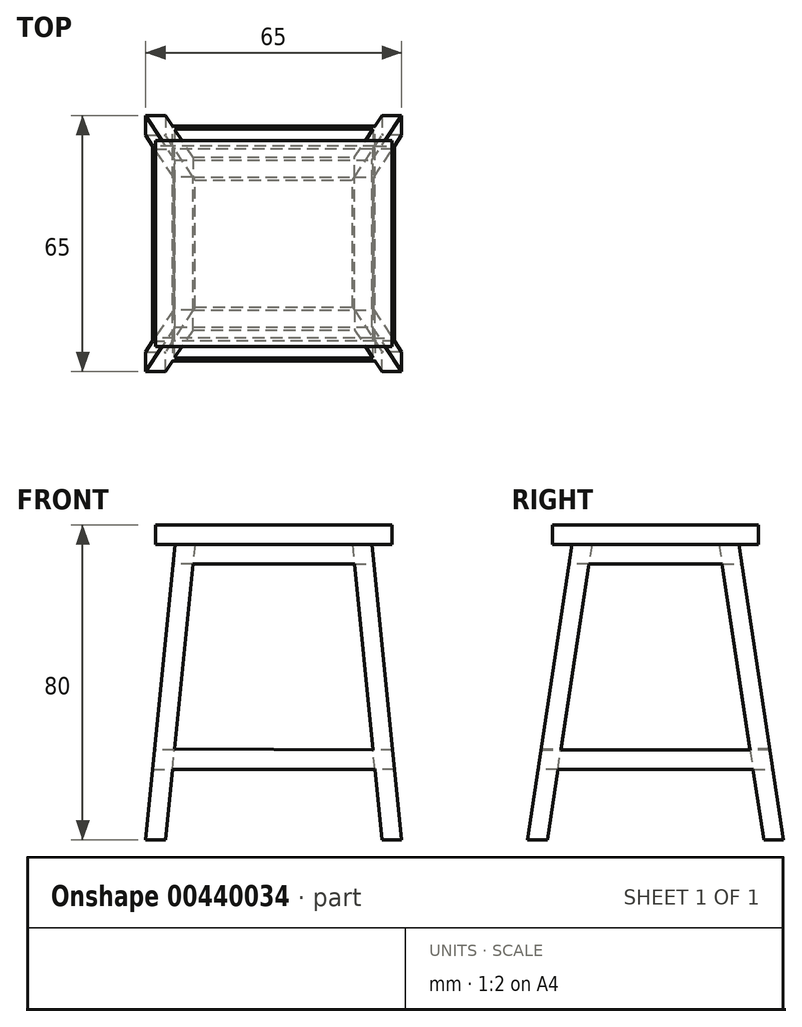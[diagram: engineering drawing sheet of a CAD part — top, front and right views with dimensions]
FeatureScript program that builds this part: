
annotation { "Feature Type Name" : "Feature", "Feature Type Description" : "" }
export const myFeature = defineFeature(function(context is Context, id is Id, definition is map)
    precondition{}
    {
        {
            var Q0;
            Q0=qCreatedBy(makeId("Top.planeOp"),FACE);
            var sketch = newSketch(context, id + "F0", { "sketchPlane" : qUnion([Q0])});
            skLineSegment(sketch, "E0.bottom", {"start": v(-30, 26.18) * mm, "end": v(30, 26.18) * mm});
            skLineSegment(sketch, "E0.top", {"start": v(-30, -26.18) * mm, "end": v(30, -26.18) * mm});
            skLineSegment(sketch, "E0.left", {"start": v(-30, 26.18) * mm, "end": v(-30, -26.18) * mm});
            skLineSegment(sketch, "E0.right", {"start": v(30, 26.18) * mm, "end": v(30, -26.18) * mm});
            skPoint(sketch, "E0.middle", {"position": v(0, 0) * mm});
            skSolve(sketch);
        }
        {
            var Q0;
            Q0 = qSketchRegion(id + "F0", true);
            extrude(context, id + "F1", {"entities" : qUnion([Q0]), "depth" : 5 * mm});
        }
        {
            var Q0;
            Q0=qCreatedBy(makeId("Top.planeOp"),FACE);
            var sketch = newSketch(context, id + "F2", { "sketchPlane" : qUnion([Q0])});
            skLineSegment(sketch, "E1.bottom", {"start": v(-25, -21.18) * mm, "end": v(-20, -21.18) * mm});
            skLineSegment(sketch, "E1.top", {"start": v(-25, -16.18) * mm, "end": v(-20, -16.18) * mm});
            skLineSegment(sketch, "E1.left", {"start": v(-25, -21.18) * mm, "end": v(-25, -16.18) * mm});
            skLineSegment(sketch, "E1.right", {"start": v(-20, -21.18) * mm, "end": v(-20, -16.18) * mm});
            skPoint(sketch, "E1.middle", {"position": v(-22.5, -18.68) * mm});
            skSolve(sketch);
        }
        {
            var Q0;
            Q0=qCreatedBy(makeId("Top.planeOp"),FACE);
            cPlane(context, id + "F3", {"entities" : qUnion([Q0]), "cplaneType" : CPlaneType.OFFSET, "offset" : 75 * mm, "oppositeDirection" : true, "width" : 150 * mm, "height" : 150 * mm});
        }
        {
            var Q0;
            Q0=qCreatedBy(id+"F3.planeOp",FACE);
            var sketch = newSketch(context, id + "F4", { "sketchPlane" : qUnion([Q0])});
            skLineSegment(sketch, "E2.bottom", {"start": v(-32.5, -32.5) * mm, "end": v(32.5, -32.5) * mm, "construction": true});
            skLineSegment(sketch, "E2.top", {"start": v(-32.5, 32.5) * mm, "end": v(32.5, 32.5) * mm, "construction": true});
            skLineSegment(sketch, "E2.left", {"start": v(-32.5, -32.5) * mm, "end": v(-32.5, 32.5) * mm, "construction": true});
            skLineSegment(sketch, "E2.right", {"start": v(32.5, -32.5) * mm, "end": v(32.5, 32.5) * mm, "construction": true});
            skPoint(sketch, "E2.middle", {"position": v(0, 0) * mm});
            skLineSegment(sketch, "E3.bottom", {"start": v(-32.5, -32.5) * mm, "end": v(-27.5, -32.5) * mm});
            skLineSegment(sketch, "E3.top", {"start": v(-32.5, -27.5) * mm, "end": v(-27.5, -27.5) * mm});
            skLineSegment(sketch, "E3.left", {"start": v(-32.5, -32.5) * mm, "end": v(-32.5, -27.5) * mm});
            skLineSegment(sketch, "E3.right", {"start": v(-27.5, -32.5) * mm, "end": v(-27.5, -27.5) * mm});
            skSolve(sketch);
        }
        {
            var Q1;
            Q1=makeQuery(id+"F2.imprint","IMPRINT",FACE,{"disambiguationData":[TD([[makeQuery(id+"F2.imprint","IMPRINT",EDGE,{"derivedFrom":sQuery(id+"F2.wireOp",EDGE,"E1.bottom")}),1.0]])]});
            var Q2;
            Q2=makeQuery(id+"F4.imprint","IMPRINT",FACE,{"disambiguationData":[TD([[makeQuery(id+"F4.imprint","IMPRINT",EDGE,{"derivedFrom":sQuery(id+"F4.wireOp",EDGE,"E3.bottom")}),1.0]])]});
            loft(context, id + "F5", {"sheetProfilesArray" : [{ "sheetProfileEntities" : qUnion([Q1]) }, { "sheetProfileEntities" : qUnion([Q2]) }]});
        }
        {
            var Q0;
            Q0=makeQuery(id+"F5.opLoft","SWEPT_BODY",BODY,{"disambiguationData":[OSD([makeQuery(id+"F2.imprint","IMPRINT",FACE,{"disambiguationData":[TD([[makeQuery(id+"F2.imprint","IMPRINT",EDGE,{"derivedFrom":sQuery(id+"F2.wireOp",EDGE,"E1.bottom")}),1.0]])]}),makeQuery(id+"F4.imprint","IMPRINT",FACE,{"disambiguationData":[TD([[makeQuery(id+"F4.imprint","IMPRINT",EDGE,{"derivedFrom":sQuery(id+"F4.wireOp",EDGE,"E3.bottom")}),1.0]])]})])]});
            var Q1;
            Q1=qCreatedBy(makeId("Right.planeOp"),FACE);
            mirror(context, id + "F6", {"entities" : qUnion([Q0]), "mirrorPlane" : qUnion([Q1])});
        }
        {
            var Q0;
            Q0=makeQuery(id+"F5.opLoft","SWEPT_BODY",BODY,{"disambiguationData":[OSD([makeQuery(id+"F2.imprint","IMPRINT",FACE,{"disambiguationData":[TD([[makeQuery(id+"F2.imprint","IMPRINT",EDGE,{"derivedFrom":sQuery(id+"F2.wireOp",EDGE,"E1.bottom")}),1.0]])]}),makeQuery(id+"F4.imprint","IMPRINT",FACE,{"disambiguationData":[TD([[makeQuery(id+"F4.imprint","IMPRINT",EDGE,{"derivedFrom":sQuery(id+"F4.wireOp",EDGE,"E3.bottom")}),1.0]])]})])]});
            var Q1;
            Q1=makeQuery(id+"F6.opPattern","COPY",BODY,{"derivedFrom":makeQuery(id+"F5.opLoft","SWEPT_BODY",BODY,{"disambiguationData":[OSD([makeQuery(id+"F2.imprint","IMPRINT",FACE,{"disambiguationData":[TD([[makeQuery(id+"F2.imprint","IMPRINT",EDGE,{"derivedFrom":sQuery(id+"F2.wireOp",EDGE,"E1.bottom")}),1.0]])]}),makeQuery(id+"F4.imprint","IMPRINT",FACE,{"disambiguationData":[TD([[makeQuery(id+"F4.imprint","IMPRINT",EDGE,{"derivedFrom":sQuery(id+"F4.wireOp",EDGE,"E3.bottom")}),1.0]])]})])]}),"instanceName":"1"});
            var Q2;
            Q2=qCreatedBy(makeId("Front.planeOp"),FACE);
            mirror(context, id + "F7", {"operationType" : NewBodyOperationType.ADD, "entities" : qUnion([Q0, Q1]), "mirrorPlane" : qUnion([Q2])});
        }
        {
            var Q0;
            Q0=makeQuery(id+"F7.opPattern","COPY",FACE,{"derivedFrom":makeQuery(id+"F6.opPattern","COPY",FACE,{"derivedFrom":makeQuery(id+"F5.opLoft","SWEPT_FACE",FACE,{"disambiguationData":[OSD([sQuery(id+"F2.wireOp",EDGE,"E1.bottom"),sQuery(id+"F2.wireOp",EDGE,"E1.top"),sQuery(id+"F2.wireOp",EDGE,"E1.right"),sQuery(id+"F4.wireOp",EDGE,"E3.bottom"),sQuery(id+"F4.wireOp",EDGE,"E3.top"),sQuery(id+"F4.wireOp",EDGE,"E3.right")])]}),"instanceName":"1"}),"instanceName":"1"});
            var sketch = newSketch(context, id + "F8", { "sketchPlane" : qUnion([Q0])});
            skLineSegment(sketch, "E4", {"start": v(-21.18, -2) * mm, "end": v(-16.18, -2) * mm});
            skLineSegment(sketch, "E5", {"start": v(-16.18, -2) * mm, "end": v(-16.92, -6.93) * mm});
            skLineSegment(sketch, "E6", {"start": v(-16.92, -6.93) * mm, "end": v(-21.92, -6.93) * mm});
            skLineSegment(sketch, "E7", {"start": v(-21.92, -6.93) * mm, "end": v(-21.18, -2) * mm});
            skSolve(sketch);
        }
        {
            var Q0;
            Q0=makeQuery(id+"F7.opPattern","COPY",FACE,{"derivedFrom":makeQuery(id+"F5.opLoft","SWEPT_FACE",FACE,{"disambiguationData":[OSD([sQuery(id+"F2.wireOp",EDGE,"E1.bottom"),sQuery(id+"F2.wireOp",EDGE,"E1.top"),sQuery(id+"F2.wireOp",EDGE,"E1.right"),sQuery(id+"F4.wireOp",EDGE,"E3.bottom"),sQuery(id+"F4.wireOp",EDGE,"E3.top"),sQuery(id+"F4.wireOp",EDGE,"E3.right")])]}),"instanceName":"1"});
            var sketch = newSketch(context, id + "F9", { "sketchPlane" : qUnion([Q0])});
            skLineSegment(sketch, "E8", {"start": v(16.18, -2) * mm, "end": v(21.18, -2) * mm});
            skLineSegment(sketch, "E9", {"start": v(21.18, -2) * mm, "end": v(21.92, -6.93) * mm});
            skLineSegment(sketch, "E10", {"start": v(21.92, -6.93) * mm, "end": v(16.92, -6.93) * mm});
            skLineSegment(sketch, "E11", {"start": v(16.92, -6.93) * mm, "end": v(16.18, -2) * mm});
            skSolve(sketch);
        }
        {
            var Q1;
            Q1=makeQuery(id+"F9.imprint","IMPRINT",FACE,{"disambiguationData":[TD([[makeQuery(id+"F9.imprint","IMPRINT",EDGE,{"derivedFrom":sQuery(id+"F9.wireOp",EDGE,"E8")}),-1.0]])]});
            var Q2;
            Q2=makeQuery(id+"F8.imprint","IMPRINT",FACE,{"disambiguationData":[TD([[makeQuery(id+"F8.imprint","IMPRINT",EDGE,{"derivedFrom":sQuery(id+"F8.wireOp",EDGE,"E4")}),1.0]])]});
            loft(context, id + "F10", {"sheetProfilesArray" : [{ "sheetProfileEntities" : qUnion([Q1]) }, { "sheetProfileEntities" : qUnion([Q2]) }]});
        }
        {
            var Q0;
            Q0=makeQuery(id+"F10.opLoft","SWEPT_BODY",BODY,{"disambiguationData":[OSD([makeQuery(id+"F8.imprint","IMPRINT",FACE,{"disambiguationData":[TD([[makeQuery(id+"F8.imprint","IMPRINT",EDGE,{"derivedFrom":sQuery(id+"F8.wireOp",EDGE,"E4")}),1.0]])]}),makeQuery(id+"F9.imprint","IMPRINT",FACE,{"disambiguationData":[TD([[makeQuery(id+"F9.imprint","IMPRINT",EDGE,{"derivedFrom":sQuery(id+"F9.wireOp",EDGE,"E8")}),-1.0]])]})])]});
            var Q1;
            Q1=qCreatedBy(makeId("Front.planeOp"),FACE);
            mirror(context, id + "F11", {"entities" : qUnion([Q0]), "mirrorPlane" : qUnion([Q1])});
        }
        {
            var Q0;
            Q0=makeQuery(id+"F7.opPattern","COPY",FACE,{"derivedFrom":makeQuery(id+"F6.opPattern","COPY",FACE,{"derivedFrom":makeQuery(id+"F5.opLoft","SWEPT_FACE",FACE,{"disambiguationData":[OSD([sQuery(id+"F2.wireOp",EDGE,"E1.top"),sQuery(id+"F2.wireOp",EDGE,"E1.left"),sQuery(id+"F2.wireOp",EDGE,"E1.right"),sQuery(id+"F4.wireOp",EDGE,"E3.top"),sQuery(id+"F4.wireOp",EDGE,"E3.left"),sQuery(id+"F4.wireOp",EDGE,"E3.right")])]}),"instanceName":"1"}),"instanceName":"1"});
            var sketch = newSketch(context, id + "F12", { "sketchPlane" : qUnion([Q0])});
            skLineSegment(sketch, "E12", {"start": v(20, -2.41) * mm, "end": v(20.5, -7.41) * mm});
            skLineSegment(sketch, "E13", {"start": v(20.5, -7.41) * mm, "end": v(25.5, -7.41) * mm});
            skLineSegment(sketch, "E14", {"start": v(25.5, -7.41) * mm, "end": v(25, -2.41) * mm});
            skLineSegment(sketch, "E15", {"start": v(25, -2.41) * mm, "end": v(20, -2.41) * mm});
            skSolve(sketch);
        }
        {
            var Q0;
            Q0=makeQuery(id+"F6.opPattern","COPY",FACE,{"derivedFrom":makeQuery(id+"F5.opLoft","SWEPT_FACE",FACE,{"disambiguationData":[OSD([sQuery(id+"F2.wireOp",EDGE,"E1.top"),sQuery(id+"F2.wireOp",EDGE,"E1.left"),sQuery(id+"F2.wireOp",EDGE,"E1.right"),sQuery(id+"F4.wireOp",EDGE,"E3.top"),sQuery(id+"F4.wireOp",EDGE,"E3.left"),sQuery(id+"F4.wireOp",EDGE,"E3.right")])]}),"instanceName":"1"});
            var sketch = newSketch(context, id + "F13", { "sketchPlane" : qUnion([Q0])});
            skLineSegment(sketch, "E16", {"start": v(-25, -2.41) * mm, "end": v(-20, -2.41) * mm});
            skLineSegment(sketch, "E17", {"start": v(-20, -2.41) * mm, "end": v(-20.5, -7.41) * mm});
            skLineSegment(sketch, "E18", {"start": v(-20.5, -7.41) * mm, "end": v(-25.5, -7.41) * mm});
            skLineSegment(sketch, "E19", {"start": v(-25.5, -7.41) * mm, "end": v(-25, -2.41) * mm});
            skSolve(sketch);
        }
        {
            var Q1;
            Q1=makeQuery(id+"F13.imprint","IMPRINT",FACE,{"disambiguationData":[TD([[makeQuery(id+"F13.imprint","IMPRINT",EDGE,{"derivedFrom":sQuery(id+"F13.wireOp",EDGE,"E16")}),-1.0]])]});
            var Q2;
            Q2=makeQuery(id+"F12.imprint","IMPRINT",FACE,{"disambiguationData":[TD([[makeQuery(id+"F12.imprint","IMPRINT",EDGE,{"derivedFrom":sQuery(id+"F12.wireOp",EDGE,"E12")}),1.0]])]});
            loft(context, id + "F14", {"sheetProfilesArray" : [{ "sheetProfileEntities" : qUnion([Q1]) }, { "sheetProfileEntities" : qUnion([Q2]) }]});
        }
        {
            var Q0;
            Q0=makeQuery(id+"F14.opLoft","SWEPT_BODY",BODY,{"disambiguationData":[OSD([makeQuery(id+"F12.imprint","IMPRINT",FACE,{"disambiguationData":[TD([[makeQuery(id+"F12.imprint","IMPRINT",EDGE,{"derivedFrom":sQuery(id+"F12.wireOp",EDGE,"E12")}),1.0]])]}),makeQuery(id+"F13.imprint","IMPRINT",FACE,{"disambiguationData":[TD([[makeQuery(id+"F13.imprint","IMPRINT",EDGE,{"derivedFrom":sQuery(id+"F13.wireOp",EDGE,"E16")}),-1.0]])]})])]});
            var Q1;
            Q1=qCreatedBy(makeId("Right.planeOp"),FACE);
            mirror(context, id + "F15", {"operationType" : NewBodyOperationType.ADD, "entities" : qUnion([Q0]), "mirrorPlane" : qUnion([Q1])});
        }
        {
            var Q0;
            {var subQ0=sQuery(id+"F4.wireOp",EDGE,"E3.right");var subQ1=sQuery(id+"F4.wireOp",EDGE,"E3.top");var subQ2=sQuery(id+"F2.wireOp",EDGE,"E1.right");var subQ3=sQuery(id+"F2.wireOp",EDGE,"E1.top");var subQ4=makeQuery(id+"F5.opLoft","SWEPT_FACE",FACE,{"disambiguationData":[OSD([sQuery(id+"F2.wireOp",EDGE,"E1.bottom"),subQ3,subQ2,sQuery(id+"F4.wireOp",EDGE,"E3.bottom"),subQ1,subQ0])]});Q0=makeQuery(id+"F15.boolean.opBoolean","MERGE",FACE,{"derivedFrom":[subQ4,makeQuery(id+"F7.opPattern","COPY",FACE,{"derivedFrom":subQ4,"instanceName":"1"}),makeQuery(id+"F15.opPattern","COPY",FACE,{"derivedFrom":makeQuery(id+"F14.opLoft","SWEPT_FACE",FACE,{"disambiguationData":[OSD([subQ3,subQ2,subQ1,subQ0,sQuery(id+"F12.wireOp",EDGE,"E12"),sQuery(id+"F12.wireOp",EDGE,"E13"),sQuery(id+"F12.wireOp",EDGE,"E15"),sQuery(id+"F13.wireOp",EDGE,"E16"),sQuery(id+"F13.wireOp",EDGE,"E17"),sQuery(id+"F13.wireOp",EDGE,"E18")])]}),"instanceName":"1"})]});}
            var sketch = newSketch(context, id + "F16", { "sketchPlane" : qUnion([Q0])});
            skLineSegment(sketch, "E20", {"start": v(16.93, -6.96) * mm, "end": v(16.85, -6.96) * mm});
            skLineSegment(sketch, "E21", {"start": v(16.85, -6.96) * mm, "end": v(16.1, -1.96) * mm});
            skLineSegment(sketch, "E22", {"start": v(16.1, -1.96) * mm, "end": v(16.93, -1.96) * mm});
            skLineSegment(sketch, "E23", {"start": v(16.93, -1.96) * mm, "end": v(16.93, -6.96) * mm});
            skLineSegment(sketch, "E24", {"start": v(24.8, -59.36) * mm, "end": v(29.8, -59.36) * mm});
            skLineSegment(sketch, "E25", {"start": v(29.8, -59.36) * mm, "end": v(29.01, -54.14) * mm});
            skLineSegment(sketch, "E26", {"start": v(29.01, -54.14) * mm, "end": v(24.01, -54.14) * mm});
            skLineSegment(sketch, "E27", {"start": v(24.01, -54.14) * mm, "end": v(24.8, -59.36) * mm});
            skLineSegment(sketch, "E28", {"start": v(32.5, -77.36) * mm, "end": v(27.5, -77.36) * mm});
            skSolve(sketch);
        }
        {
            var Q0;
            {var subQ0=sQuery(id+"F4.wireOp",EDGE,"E3.right");var subQ1=sQuery(id+"F4.wireOp",EDGE,"E3.top");var subQ2=sQuery(id+"F2.wireOp",EDGE,"E1.right");var subQ3=sQuery(id+"F2.wireOp",EDGE,"E1.top");var subQ4=makeQuery(id+"F6.opPattern","COPY",FACE,{"derivedFrom":makeQuery(id+"F5.opLoft","SWEPT_FACE",FACE,{"disambiguationData":[OSD([sQuery(id+"F2.wireOp",EDGE,"E1.bottom"),subQ3,subQ2,sQuery(id+"F4.wireOp",EDGE,"E3.bottom"),subQ1,subQ0])]}),"instanceName":"1"});Q0=makeQuery(id+"F15.boolean.opBoolean","MERGE",FACE,{"derivedFrom":[subQ4,makeQuery(id+"F7.opPattern","COPY",FACE,{"derivedFrom":subQ4,"instanceName":"1"}),makeQuery(id+"F14.opLoft","SWEPT_FACE",FACE,{"disambiguationData":[OSD([subQ3,subQ2,subQ1,subQ0,sQuery(id+"F12.wireOp",EDGE,"E12"),sQuery(id+"F12.wireOp",EDGE,"E13"),sQuery(id+"F12.wireOp",EDGE,"E15"),sQuery(id+"F13.wireOp",EDGE,"E16"),sQuery(id+"F13.wireOp",EDGE,"E17"),sQuery(id+"F13.wireOp",EDGE,"E18")])]})]});}
            var sketch = newSketch(context, id + "F17", { "sketchPlane" : qUnion([Q0])});
            skLineSegment(sketch, "E29", {"start": v(-24.8, -59.36) * mm, "end": v(-29.8, -59.36) * mm});
            skLineSegment(sketch, "E30", {"start": v(-29.8, -59.36) * mm, "end": v(-29.05, -54.42) * mm});
            skLineSegment(sketch, "E31", {"start": v(-29.05, -54.42) * mm, "end": v(-24.05, -54.42) * mm});
            skLineSegment(sketch, "E32", {"start": v(-24.05, -54.42) * mm, "end": v(-24.8, -59.36) * mm});
            skSolve(sketch);
        }
        {
            var Q1;
            Q1=makeQuery(id+"F17.imprint","IMPRINT",FACE,{"disambiguationData":[TD([[makeQuery(id+"F17.imprint","IMPRINT",EDGE,{"derivedFrom":sQuery(id+"F17.wireOp",EDGE,"E29")}),-1.0]])]});
            var Q2;
            Q2=makeQuery(id+"F16.imprint","IMPRINT",FACE,{"disambiguationData":[TD([[makeQuery(id+"F16.imprint","IMPRINT",EDGE,{"derivedFrom":sQuery(id+"F16.wireOp",EDGE,"E24")}),1.0]])]});
            loft(context, id + "F18", {"sheetProfilesArray" : [{ "sheetProfileEntities" : qUnion([Q1]) }, { "sheetProfileEntities" : qUnion([Q2]) }]});
        }
        {
            var Q0;
            Q0=makeQuery(id+"F18.opLoft","SWEPT_BODY",BODY,{"disambiguationData":[OSD([makeQuery(id+"F16.imprint","IMPRINT",FACE,{"disambiguationData":[TD([[makeQuery(id+"F16.imprint","IMPRINT",EDGE,{"derivedFrom":sQuery(id+"F16.wireOp",EDGE,"E24")}),1.0]])]}),makeQuery(id+"F17.imprint","IMPRINT",FACE,{"disambiguationData":[TD([[makeQuery(id+"F17.imprint","IMPRINT",EDGE,{"derivedFrom":sQuery(id+"F17.wireOp",EDGE,"E29")}),-1.0]])]})])]});
            var Q1;
            Q1=qCreatedBy(makeId("Front.planeOp"),FACE);
            mirror(context, id + "F19", {"operationType" : NewBodyOperationType.ADD, "entities" : qUnion([Q0]), "mirrorPlane" : qUnion([Q1])});
        }
        {
            var Q0;
            {var subQ0=sQuery(id+"F4.wireOp",EDGE,"E3.right");var subQ1=sQuery(id+"F4.wireOp",EDGE,"E3.top");var subQ2=sQuery(id+"F2.wireOp",EDGE,"E1.right");var subQ3=sQuery(id+"F2.wireOp",EDGE,"E1.top");var subQ4=makeQuery(id+"F5.opLoft","SWEPT_FACE",FACE,{"disambiguationData":[OSD([subQ3,sQuery(id+"F2.wireOp",EDGE,"E1.left"),subQ2,subQ1,sQuery(id+"F4.wireOp",EDGE,"E3.left"),subQ0])]});Q0=makeQuery(id+"F19.boolean.opBoolean","MERGE",FACE,{"derivedFrom":[makeQuery(id+"F7.opPattern","COPY",FACE,{"derivedFrom":subQ4,"instanceName":"1"}),makeQuery(id+"F7.opPattern","COPY",FACE,{"derivedFrom":makeQuery(id+"F6.opPattern","COPY",FACE,{"derivedFrom":subQ4,"instanceName":"1"}),"instanceName":"1"}),makeQuery(id+"F18.opLoft","SWEPT_FACE",FACE,{"disambiguationData":[OSD([subQ3,subQ2,subQ1,subQ0,sQuery(id+"F16.wireOp",EDGE,"E24"),sQuery(id+"F16.wireOp",EDGE,"E26"),sQuery(id+"F16.wireOp",EDGE,"E27"),sQuery(id+"F17.wireOp",EDGE,"E29"),sQuery(id+"F17.wireOp",EDGE,"E31"),sQuery(id+"F17.wireOp",EDGE,"E32")])]})]});}
            var sketch = newSketch(context, id + "F20", { "sketchPlane" : qUnion([Q0])});
            skLineSegment(sketch, "E33", {"start": v(25.22, -55.17) * mm, "end": v(25.7, -60.15) * mm});
            skLineSegment(sketch, "E34", {"start": v(25.7, -60.15) * mm, "end": v(30.7, -60.15) * mm});
            skLineSegment(sketch, "E35", {"start": v(30.7, -60.15) * mm, "end": v(30.22, -55.17) * mm});
            skLineSegment(sketch, "E36", {"start": v(30.22, -55.17) * mm, "end": v(25.22, -55.17) * mm});
            skSolve(sketch);
        }
        {
            var Q0;
            {var subQ0=sQuery(id+"F4.wireOp",EDGE,"E3.right");var subQ1=sQuery(id+"F4.wireOp",EDGE,"E3.top");var subQ2=sQuery(id+"F2.wireOp",EDGE,"E1.right");var subQ3=sQuery(id+"F2.wireOp",EDGE,"E1.top");var subQ4=makeQuery(id+"F5.opLoft","SWEPT_FACE",FACE,{"disambiguationData":[OSD([subQ3,sQuery(id+"F2.wireOp",EDGE,"E1.left"),subQ2,subQ1,sQuery(id+"F4.wireOp",EDGE,"E3.left"),subQ0])]});Q0=makeQuery(id+"F19.boolean.opBoolean","MERGE",FACE,{"derivedFrom":[subQ4,makeQuery(id+"F6.opPattern","COPY",FACE,{"derivedFrom":subQ4,"instanceName":"1"}),makeQuery(id+"F19.opPattern","COPY",FACE,{"derivedFrom":makeQuery(id+"F18.opLoft","SWEPT_FACE",FACE,{"disambiguationData":[OSD([subQ3,subQ2,subQ1,subQ0,sQuery(id+"F16.wireOp",EDGE,"E24"),sQuery(id+"F16.wireOp",EDGE,"E26"),sQuery(id+"F16.wireOp",EDGE,"E27"),sQuery(id+"F17.wireOp",EDGE,"E29"),sQuery(id+"F17.wireOp",EDGE,"E31"),sQuery(id+"F17.wireOp",EDGE,"E32")])]}),"instanceName":"1"})]});}
            var sketch = newSketch(context, id + "F21", { "sketchPlane" : qUnion([Q0])});
            skLineSegment(sketch, "E37", {"start": v(-25.7, -60.15) * mm, "end": v(-25.22, -55.17) * mm});
            skLineSegment(sketch, "E38", {"start": v(-25.22, -55.17) * mm, "end": v(-30.22, -55.17) * mm});
            skLineSegment(sketch, "E39", {"start": v(-30.22, -55.17) * mm, "end": v(-30.7, -60.15) * mm});
            skLineSegment(sketch, "E40", {"start": v(-30.7, -60.15) * mm, "end": v(-25.7, -60.15) * mm});
            skSolve(sketch);
        }
        {
            var Q1;
            Q1=makeQuery(id+"F21.imprint","IMPRINT",FACE,{"disambiguationData":[TD([[makeQuery(id+"F21.imprint","IMPRINT",EDGE,{"derivedFrom":sQuery(id+"F21.wireOp",EDGE,"E37")}),1.0]])]});
            var Q2;
            Q2=makeQuery(id+"F20.imprint","IMPRINT",FACE,{"disambiguationData":[TD([[makeQuery(id+"F20.imprint","IMPRINT",EDGE,{"derivedFrom":sQuery(id+"F20.wireOp",EDGE,"E33")}),1.0]])]});
            loft(context, id + "F22", {"sheetProfilesArray" : [{ "sheetProfileEntities" : qUnion([Q1]) }, { "sheetProfileEntities" : qUnion([Q2]) }]});
        }
        {
            var Q0;
            Q0=makeQuery(id+"F22.opLoft","SWEPT_BODY",BODY,{"disambiguationData":[OSD([makeQuery(id+"F20.imprint","IMPRINT",FACE,{"disambiguationData":[TD([[makeQuery(id+"F20.imprint","IMPRINT",EDGE,{"derivedFrom":sQuery(id+"F20.wireOp",EDGE,"E33")}),1.0]])]}),makeQuery(id+"F21.imprint","IMPRINT",FACE,{"disambiguationData":[TD([[makeQuery(id+"F21.imprint","IMPRINT",EDGE,{"derivedFrom":sQuery(id+"F21.wireOp",EDGE,"E37")}),1.0]])]})])]});
            var Q1;
            Q1=qCreatedBy(makeId("Right.planeOp"),FACE);
            mirror(context, id + "F23", {"operationType" : NewBodyOperationType.ADD, "entities" : qUnion([Q0]), "mirrorPlane" : qUnion([Q1])});
        }
    });
